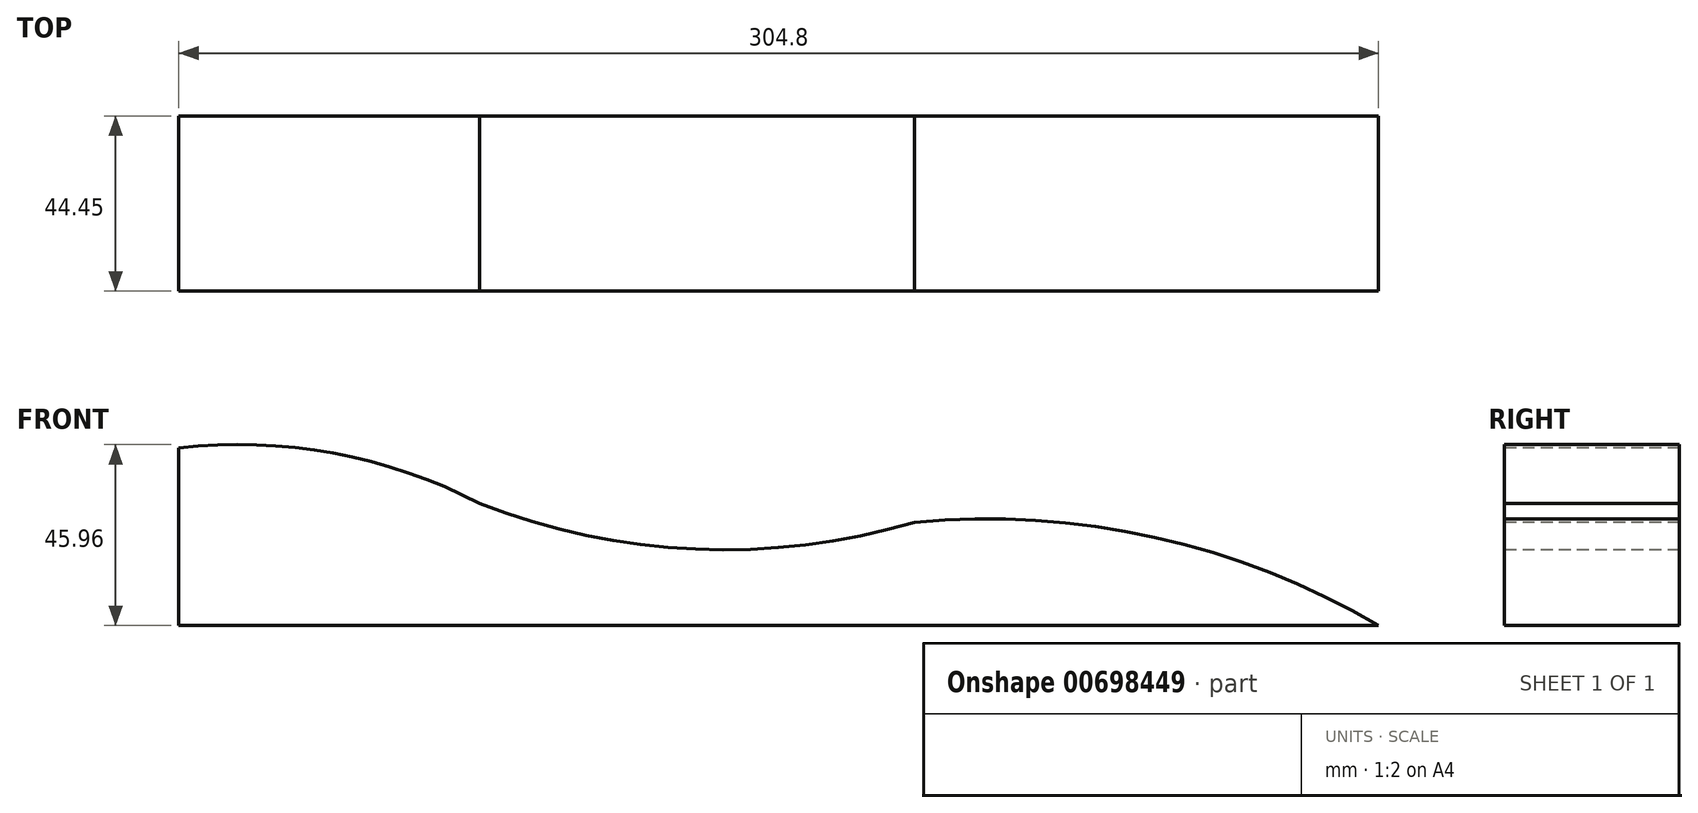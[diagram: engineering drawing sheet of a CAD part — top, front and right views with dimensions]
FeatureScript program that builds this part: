
annotation { "Feature Type Name" : "Feature", "Feature Type Description" : "" }
export const myFeature = defineFeature(function(context is Context, id is Id, definition is map)
    precondition{}
    {
        {
            var Q0;
            Q0=qCreatedBy(makeId("Front.planeOp"),FACE);
            var sketch = newSketch(context, id + "F0", { "sketchPlane" : qUnion([Q0])});
            skLineSegment(sketch, "E0", {"start": v(0, 0) * mm, "end": v(304.8, 0) * mm});
            skLineSegment(sketch, "E1", {"start": v(304.8, 0) * mm, "end": v(304.8, 19.05) * mm});
            skLineSegment(sketch, "E2", {"start": v(304.8, 19.05) * mm, "end": v(0, 69.85) * mm});
            skLineSegment(sketch, "E3", {"start": v(0, 69.85) * mm, "end": v(0, 0) * mm});
            skSolve(sketch);
        }
        {
            var Q0;
            Q0=makeQuery(id+"F0.imprint","IMPRINT",FACE,{"disambiguationData":[TD([[makeQuery(id+"F0.imprint","IMPRINT",EDGE,{"derivedFrom":sQuery(id+"F0.wireOp",EDGE,"E0")}),1.0]])]});
            extrude(context, id + "F1", {"entities" : qUnion([Q0]), "oppositeDirection" : true, "depth" : 44.45 * mm, "offsetDistance" : 25.4 * mm});
        }
        {
            var Q0;
            Q0=makeQuery(id+"F1.opExtrude","CAP_FACE",FACE,{"disambiguationData":[OSD([sQuery(id+"F0.wireOp",EDGE,"E0"),sQuery(id+"F0.wireOp",EDGE,"E1"),sQuery(id+"F0.wireOp",EDGE,"E2"),sQuery(id+"F0.wireOp",EDGE,"E3")])],"isStart":true});
            var sketch = newSketch(context, id + "F2", { "sketchPlane" : qUnion([Q0])});
            skArc(sketch, "E4", {"start": v(76.42, 31) * mm, "mid": v(39.27, 43.78) * mm, "end": v(0, 45.07) * mm});
            skArc(sketch, "E5", {"start": v(76.42, 31) * mm, "mid": v(131.27, 19.38) * mm, "end": v(186.91, 26.2) * mm});
            skArc(sketch, "E6", {"start": v(304.8, 0) * mm, "mid": v(247.92, 22.37) * mm, "end": v(186.91, 26.2) * mm});
            skSolve(sketch);
        }
        {
            var Q0;
            Q0 = qSketchRegion(id + "F2", true);
            var Q1;
            {var subQ0=sQuery(id+"F2.wireOp",EDGE,"E4");Q1=makeQuery(id+"F2.imprint","IMPRINT",FACE,{"disambiguationData":[TD([[makeQuery(id+"F2.imprint","IMPRINT",EDGE,{"derivedFrom":subQ0}),-1.0]])]});}
            extrude(context, id + "F3", {"entities" : qUnion([Q0, Q1]), "operationType" : NewBodyOperationType.REMOVE, "oppositeDirection" : true, "depth" : 50.8 * mm, "offsetDistance" : 25.4 * mm});
        }
    });
